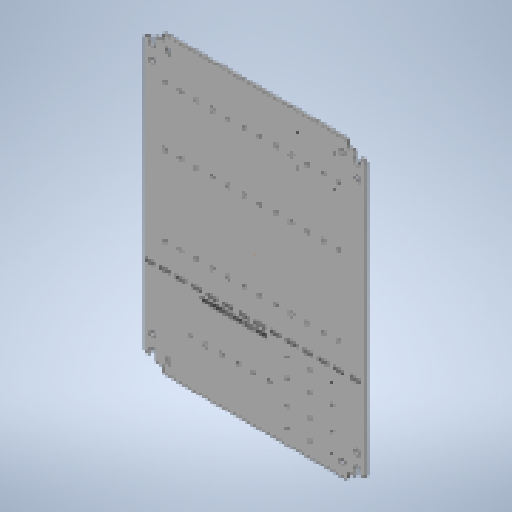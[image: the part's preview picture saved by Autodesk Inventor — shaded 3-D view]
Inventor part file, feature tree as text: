
AUTODESK INVENTOR PART (.ipt)
format: ipt  version: 2023 (Build 270158030, 158C)  size: 946,176 bytes
history: native  units: mm
features: reference x18, other x15, extrude x4, sketch x4, mirror x2
ambient origin geometry x8: Origin, YZ Plane, XZ Plane, XY Plane, X Axis, Y Axis, Z Axis, Center Point
bodies: Solid1 (feature_tree)
feature tree (43):
  other  "Blocks"
  extrude  "Extrusion1"  Depth=465.0mm
  extrude  "Extrusion2"  Depth=175.0mm
  mirror  "Mirror1"
  mirror  "Mirror2"
  extrude  "Extrusion3"  Depth=3.0mm
  extrude  "Extrusion4"  Depth=1.0mm
  sketch  "Sketch1"  dims[d0=350.0mm d1=465.0mm]
  sketch  "Sketch3"  dims[d2=232.5mm d3=175.0mm]
  sketch  "Sketch4"  dims[d4=3.0mm d5=0.0mm d7=465.0mm]
  reference  "Reference1"
  reference  "Reference2"
  reference  "Reference3"
  reference  "Reference4"
  reference  "Reference5"
  reference  "Reference6"
  reference  "Reference7"
  reference  "Reference8"
  reference  "Reference9"
  reference  "Reference10"
  reference  "Reference11"
  reference  "Reference12"
  reference  "Reference13"
  reference  "Reference14"
  reference  "Reference15"
  reference  "Reference16"
  reference  "Reference17"
  reference  "Reference18"
  sketch  "Sketch5"  dims[d8=350.0mm d9=28.5mm d10=10.0mm d11=6.0mm d12=19.0mm d14=5.0mm d15=11.0mm d16=45.0deg d17=3.0mm d18=3.0mm d19=45.0deg d20=0.0mm d21=0.0mm d22=8.4mm d23=13.0mm d24=13.5mm d25=45.5mm d26=37.5mm d27=21.0mm d28=5.2mm d29=5.8mm d30=5.8mm d31=25.0mm d32=120.0mm d34=25.0mm d35=20.0mm d37=125.0mm d40=5.2mm d41=5.8mm d42=60.0mm d44=25.0mm d45=10.0mm d47=10.0mm d49=3.2mm d50=30.0mm d52=35.0mm d53=20.0mm d55=97.5mm d58=20.0mm d60=92.0mm d61=120.0mm d63=25.0mm d66=0.0mm d67=0.0mm d68=4.0mm d69=15.0mm d70=145.0mm d71=100.0mm d73=25.0mm d74=10.0mm d76=10.0mm d81=50.0mm d83=25.0mm d84=10.0mm d86=10.0mm d88=1.0mm d89=0.0mm d142=2.0mm d146=1.0mm d148=19.5mm d150=1.0mm d155=50.0mm d157=19.5mm d158=10.0mm d160=10.0mm d165=100.0mm d167=10.0mm d169=50.0mm d171=10.0mm d173=50.0mm d175=10.0mm d176=50.0mm d177=62.0mm d178=20.0mm d179=1.0mm d180=1.0mm d181=1.0mm d182=1.0mm d183=1.0mm d184=1.0mm]
  other  "high voltage"
  other  "<userpath>\Documents\0004-inventor\Inventor_Projects\electronics-enclosure\enclosure.iam"
  other  "enclosure.iam"
  other  "Raspberry Pi 4 Model B:1"
  other  "PCB, RPi4ModelB_1"
  other  "DIN-rail:1"
  other  "DIN-rail-short:1"
  other  "solid state relay_MIR:1"
  other  "solid state relay_MIR:2"
  other  "solid state relay_MIR:3"
  other  "solid state relay:1"
  other  "solid state relay:3"
  other  "solid state relay:4"
  other  "high voltage:1"
